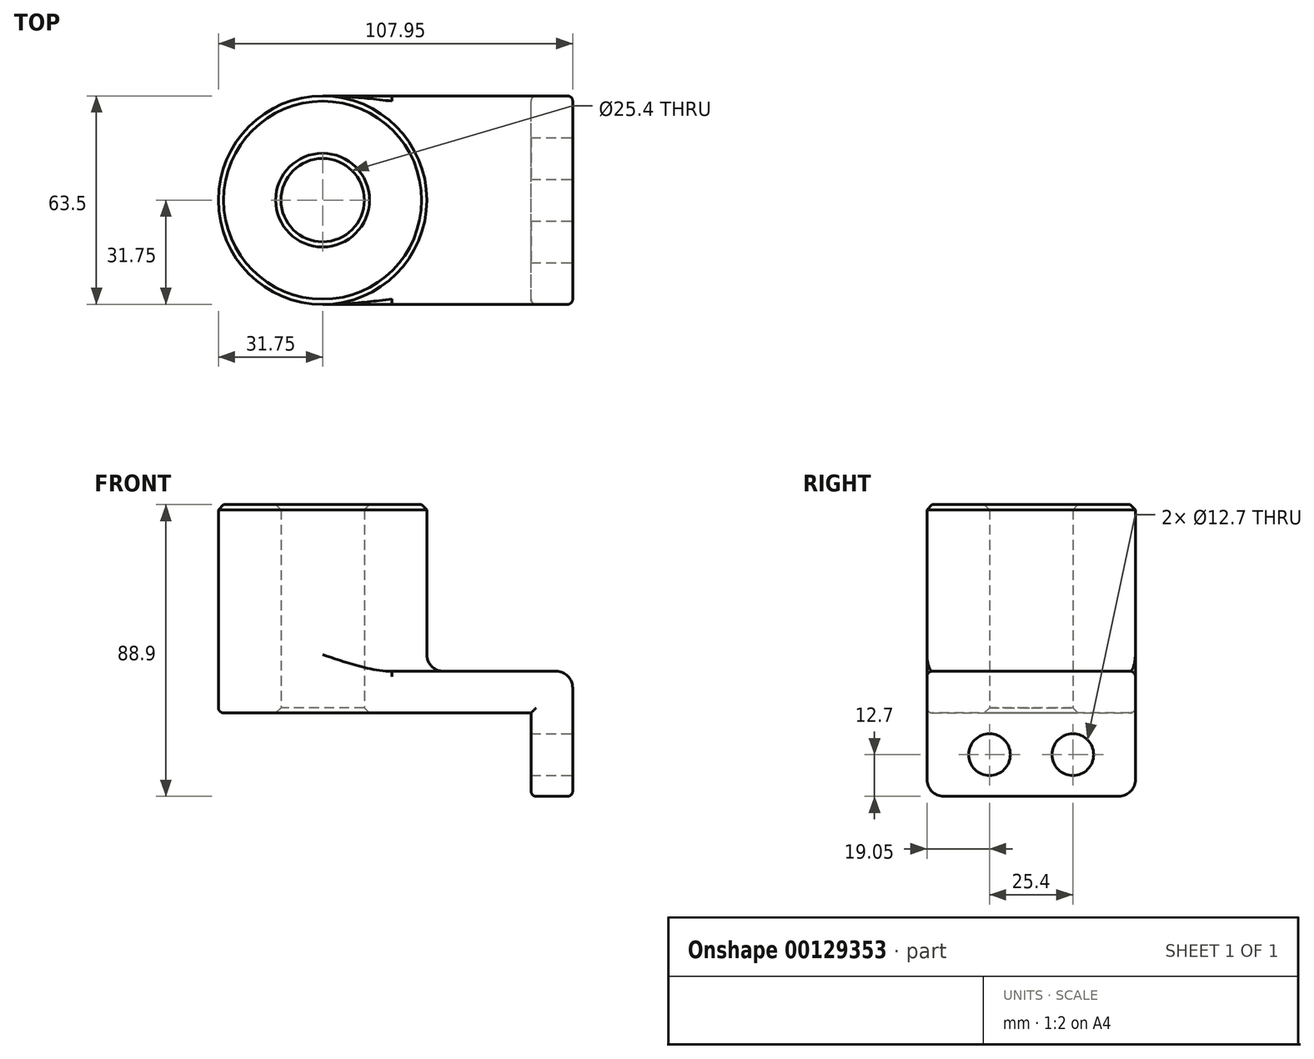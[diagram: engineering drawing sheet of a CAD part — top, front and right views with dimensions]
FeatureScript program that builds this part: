
annotation { "Feature Type Name" : "Feature", "Feature Type Description" : "" }
export const myFeature = defineFeature(function(context is Context, id is Id, definition is map)
    precondition{}
    {
        {
            var Q0;
            Q0=qCreatedBy(makeId("Top.planeOp"),FACE);
            var sketch = newSketch(context, id + "F0", { "sketchPlane" : qUnion([Q0])});
            skLineSegment(sketch, "E0.bottom", {"start": v(-38.1, 31.75) * mm, "end": v(38.1, 31.75) * mm});
            skLineSegment(sketch, "E0.top", {"start": v(-38.1, -31.75) * mm, "end": v(38.1, -31.75) * mm});
            skLineSegment(sketch, "E0.left", {"start": v(-38.1, 31.75) * mm, "end": v(-38.1, -31.75) * mm});
            skLineSegment(sketch, "E0.right", {"start": v(38.1, 31.75) * mm, "end": v(38.1, -31.75) * mm});
            skPoint(sketch, "E0.middle", {"position": v(0, 0) * mm});
            skCircle(sketch, "E1", {"center": v(-38.1, 0) * mm, "radius": 31.75 * mm});
            skCircle(sketch, "E2", {"center": v(-38.1, 0) * mm, "radius": 12.7 * mm});
            skSolve(sketch);
        }
        {
            var Q0;
            Q0 = qSketchRegion(id + "F0", true);
            extrude(context, id + "F1", {"entities" : qUnion([Q0]), "depth" : 12.7 * mm});
        }
        {
            var Q0;
            {var subQ1=sQuery(id+"F0.wireOp",EDGE,"E0.left");var subQ3=sQuery(id+"F0.wireOp",EDGE,"E2");var subQ4=makeQuery(id+"F0.imprint","INTERSECT",VERTEX,{"disambiguationData":[OD(0.0)],"derivedFrom":[subQ1,subQ3]});Q0=makeQuery(id+"F0.imprint","IMPRINT",FACE,{"disambiguationData":[TD([[makeQuery(id+"F0.imprint","IMPRINT",EDGE,{"disambiguationData":[TD([[subQ4,-1.0]])],"derivedFrom":subQ3}),-1.0]])]});}
            var Q1;
            {var subQ1=sQuery(id+"F0.wireOp",EDGE,"E0.left");var subQ3=sQuery(id+"F0.wireOp",EDGE,"E2");var subQ4=makeQuery(id+"F0.imprint","INTERSECT",VERTEX,{"disambiguationData":[OD(0.0)],"derivedFrom":[subQ1,subQ3]});Q1=makeQuery(id+"F0.imprint","IMPRINT",FACE,{"disambiguationData":[TD([[makeQuery(id+"F0.imprint","IMPRINT",EDGE,{"disambiguationData":[TD([[subQ4,1.0]])],"derivedFrom":subQ3}),-1.0]])]});}
            extrude(context, id + "F2", {"entities" : qUnion([Q0, Q1]), "operationType" : NewBodyOperationType.ADD, "depth" : 63.5 * mm});
        }
        {
            var Q0;
            Q0=makeQuery(id+"F1.opExtrude","SWEPT_FACE",FACE,{"disambiguationData":[OSD([sQuery(id+"F0.wireOp",EDGE,"E0.right")])]});
            var sketch = newSketch(context, id + "F3", { "sketchPlane" : qUnion([Q0])});
            skLineSegment(sketch, "E3.bottom", {"start": v(-31.75, 12.7) * mm, "end": v(31.75, 12.7) * mm});
            skLineSegment(sketch, "E3.top", {"start": v(-31.75, -25.4) * mm, "end": v(31.75, -25.4) * mm});
            skLineSegment(sketch, "E3.left", {"start": v(-31.75, 12.7) * mm, "end": v(-31.75, -25.4) * mm});
            skLineSegment(sketch, "E3.right", {"start": v(31.75, 12.7) * mm, "end": v(31.75, -25.4) * mm});
            skCircle(sketch, "E4", {"center": v(-12.7, -12.7) * mm, "radius": 6.35 * mm});
            skLineSegment(sketch, "E5", {"start": v(0, 0) * mm, "end": v(0, -25.4) * mm, "construction": true});
            skCircle(sketch, "E6.MirrorC", {"center": v(12.7, -12.7) * mm, "radius": 6.35 * mm});
            skSolve(sketch);
        }
        {
            var Q0;
            Q0 = qSketchRegion(id + "F3", true);
            extrude(context, id + "F4", {"entities" : qUnion([Q0]), "operationType" : NewBodyOperationType.ADD, "oppositeDirection" : true, "depth" : 12.7 * mm});
        }
        {
            var Q0;
            {var subQ0=sQuery(id+"F0.wireOp",EDGE,"E1");Q0=makeQuery(id+"F2.boolean.opBoolean","INTERSECT",EDGE,{"derivedFrom":[makeQuery(id+"F1.opExtrude","CAP_FACE",FACE,{"disambiguationData":[OSD([sQuery(id+"F0.wireOp",EDGE,"E0.bottom"),sQuery(id+"F0.wireOp",EDGE,"E0.top"),sQuery(id+"F0.wireOp",EDGE,"E0.right"),subQ0,sQuery(id+"F0.wireOp",EDGE,"E2")])],"isStart":false}),makeQuery(id+"F2.opExtrude","SWEPT_FACE",FACE,{"disambiguationData":[OSD([subQ0])]})]});}
            var Q1;
            Q1=makeQuery(id+"F1.opExtrude","CAP_EDGE",EDGE,{"disambiguationData":[OSD([sQuery(id+"F0.wireOp",EDGE,"E0.right")])],"isStart":false});
            var Q2;
            Q2=makeQuery(id+"F4.opExtrude","SWEPT_EDGE",EDGE,{"disambiguationData":[OSD([sQuery(id+"F3.wireOp",EDGE,"E3.top"),sQuery(id+"F3.wireOp",EDGE,"E3.right")])]});
            var Q3;
            Q3=makeQuery(id+"F4.opExtrude","SWEPT_EDGE",EDGE,{"disambiguationData":[OSD([sQuery(id+"F3.wireOp",EDGE,"E3.top"),sQuery(id+"F3.wireOp",EDGE,"E3.left")])]});
            fillet(context, id + "F5", {"entities" : qUnion([Q0, Q1, Q2, Q3]), "radius" : 5.08 * mm, "tangentPropagation" : true, "allowEdgeOverflow" : false});
        }
        {
            var Q0;
            Q0=makeQuery(id+"F1.opExtrude","CAP_EDGE",EDGE,{"disambiguationData":[OSD([sQuery(id+"F0.wireOp",EDGE,"E0.top")])],"isStart":false});
            var Q1;
            Q1=makeQuery(id+"F1.opExtrude","CAP_EDGE",EDGE,{"disambiguationData":[OSD([sQuery(id+"F0.wireOp",EDGE,"E0.top")])],"isStart":true});
            var Q2;
            Q2=makeQuery(id+"F4.opExtrude","CAP_EDGE",EDGE,{"disambiguationData":[OSD([sQuery(id+"F3.wireOp",EDGE,"E3.left")])],"isStart":false});
            fillet(context, id + "F6", {"entities" : qUnion([Q0, Q1, Q2]), "radius" : 1.59 * mm, "tangentPropagation" : true, "allowEdgeOverflow" : false});
        }
        {
            var Q0;
            {var subQ0=sQuery(id+"F0.wireOp",EDGE,"E2");Q0=makeQuery(id+"F2.boolean.opBoolean","MERGE",FACE,{"derivedFrom":[makeQuery(id+"F1.opExtrude","SWEPT_FACE",FACE,{"disambiguationData":[OSD([subQ0])]}),makeQuery(id+"F2.opExtrude","SWEPT_FACE",FACE,{"disambiguationData":[OSD([subQ0])]})]});}
            chamfer(context, id + "F7", {"entities" : qUnion([Q0]), "width" : 1.59 * mm, "tangentPropagation" : true});
        }
        {
            var Q0;
            Q0=makeQuery(id+"F2.opExtrude","CAP_EDGE",EDGE,{"disambiguationData":[OSD([sQuery(id+"F0.wireOp",EDGE,"E1")])],"isStart":false});
            chamfer(context, id + "F8", {"entities" : qUnion([Q0]), "width" : 1.59 * mm, "tangentPropagation" : true});
        }
    });
